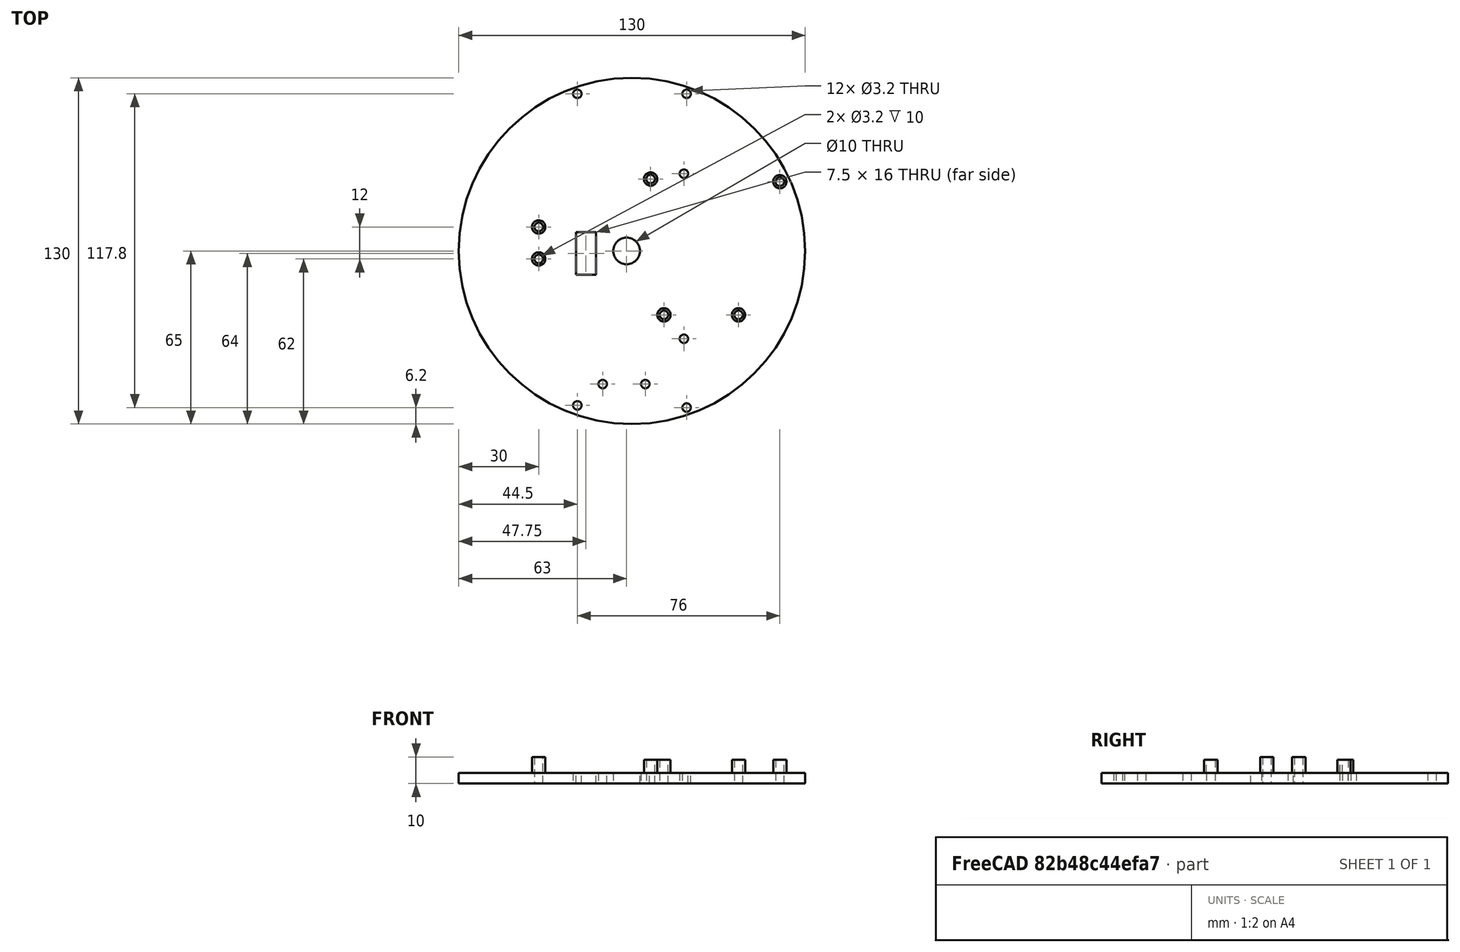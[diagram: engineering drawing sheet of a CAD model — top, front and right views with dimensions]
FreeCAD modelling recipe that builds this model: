
FCSTD DOCUMENT  (FreeCAD 0.21R33668 +26 (Git))
Label: plataformaSuperior
License: All rights reserved
LicenseURL: https://en.wikipedia.org/wiki/All_rights_reserved
objects: Part::Cylinder×26, Part::MultiFuse×10, Part::Cut×6, Part::Box×1, Mesh::Feature×1
note: 43 computed .brp shape members not serialized (recipe doc carries the construction recipe); baked Part::Feature solids carry a one-line shape summary decoded from their .brp

FEATURE [Part::Box] Box027  label="Cubo027"
  AttacherType = Attacher::AttachEngine3D
  Height = 7
  Length = 7.5
  Placement = pos=(-25,-9,46) rot=(0,0,1;0rad)
  Width = 16
FEATURE [Part::Cylinder] Cylinder034  label="Cilindro034"
  Angle = 360
  AttacherType = Attacher::AttachEngine3D
  FirstAngle = 0
  Height = 10
  Placement = pos=(-27,-22,24) rot=(0,0,1;0rad)
  Radius = 1.6
  SecondAngle = 0
FEATURE [Part::Cylinder] Cylinder035  label="Cilindro035"
  Angle = 360
  AttacherType = Attacher::AttachEngine3D
  FirstAngle = 0
  Height = 10
  Placement = pos=(24,11,24) rot=(0,0,1;0rad)
  Radius = 1.6
  SecondAngle = 0
FEATURE [Part::Cylinder] Cylinder036  label="Cilindro036"
  Angle = 360
  AttacherType = Attacher::AttachEngine3D
  FirstAngle = 0
  Height = 10
  Placement = pos=(24,-17,24) rot=(0,0,1;0rad)
  Radius = 1.6
  SecondAngle = 0
FEATURE [Part::Cylinder] Cylinder037  label="Cilindro037"
  Angle = 360
  AttacherType = Attacher::AttachEngine3D
  FirstAngle = 0
  Height = 10
  Placement = pos=(-26,26.5,24) rot=(0,0,1;0rad)
  Radius = 1.6
  SecondAngle = 0
FEATURE [Part::Cylinder] Cylinder038  label="Cilindro038"
  Angle = 360
  AttacherType = Attacher::AttachEngine3D
  FirstAngle = 0
  Height = 6
  Placement = pos=(-27,-22,28) rot=(0,0,1;0rad)
  Radius = 2.5
  SecondAngle = 0
FEATURE [Part::Cylinder] Cylinder039  label="Cilindro039"
  Angle = 360
  AttacherType = Attacher::AttachEngine3D
  FirstAngle = 0
  Height = 6
  Placement = pos=(24,11,28) rot=(0,0,1;0rad)
  Radius = 2.5
  SecondAngle = 0
FEATURE [Part::Cylinder] Cylinder040  label="Cilindro040"
  Angle = 360
  AttacherType = Attacher::AttachEngine3D
  FirstAngle = 0
  Height = 6
  Placement = pos=(24,-17,28) rot=(0,0,1;0rad)
  Radius = 2.5
  SecondAngle = 0
FEATURE [Part::Cylinder] Cylinder041  label="Cilindro041"
  Angle = 360
  AttacherType = Attacher::AttachEngine3D
  FirstAngle = 0
  Height = 6
  Placement = pos=(-26,26.5,28) rot=(0,0,1;0rad)
  Radius = 2.5
  SecondAngle = 0
FEATURE [Part::Cylinder] Cylinder042  label="Cilindro042"
  Angle = 360
  AttacherType = Attacher::AttachEngine3D
  FirstAngle = 0
  Height = 6
  Placement = pos=(35,9,28) rot=(0,0,1;0rad)
  Radius = 2.5
  SecondAngle = 0
FEATURE [Part::Cylinder] Cylinder044  label="Cilindro044"
  Angle = 360
  AttacherType = Attacher::AttachEngine3D
  FirstAngle = 0
  Height = 6
  Placement = pos=(35,-3,28) rot=(0,0,1;0rad)
  Radius = 2.5
  SecondAngle = 0
FEATURE [Part::Cylinder] Cylinder099  label="Cilindro099"
  Angle = 360
  AttacherType = Attacher::AttachEngine3D
  FirstAngle = 0
  Height = 4
  Placement = pos=(-4,0,49) rot=(0,0,1;0rad)
  Radius = 65
  SecondAngle = 0
FEATURE [Part::Cylinder] Cylinder100  label="Cilindro100"
  Angle = 360
  AttacherType = Attacher::AttachEngine3D
  FirstAngle = 0
  Height = 50
  Placement = pos=(16.5,-58.8,-17) rot=(0,0,1;0rad)
  Radius = 1.6
  SecondAngle = 0
FEATURE [Part::Cylinder] Cylinder101  label="Cilindro101"
  Angle = 360
  AttacherType = Attacher::AttachEngine3D
  FirstAngle = 0
  Height = 50
  Placement = pos=(16.5,59,-17) rot=(0,0,1;0rad)
  Radius = 1.6
  SecondAngle = 0
FEATURE [Part::Cylinder] Cylinder102  label="Cilindro102"
  Angle = 360
  AttacherType = Attacher::AttachEngine3D
  FirstAngle = 0
  Height = 50
  Placement = pos=(-24.5,59,-17) rot=(0,0,1;0rad)
  Radius = 1.6
  SecondAngle = 0
FEATURE [Part::Cylinder] Cylinder103  label="Cilindro103"
  Angle = 360
  AttacherType = Attacher::AttachEngine3D
  FirstAngle = 0
  Height = 50
  Placement = pos=(-24.5,-58,-17) rot=(0,0,1;0rad)
  Radius = 1.6
  SecondAngle = 0
FEATURE [Part::Cylinder] Cylinder104  label="Cilindro104"
  Angle = 360
  AttacherType = Attacher::AttachEngine3D
  FirstAngle = 0
  Height = 20
  Placement = pos=(-6,0,43) rot=(0,0,1;0rad)
  Radius = 5
  SecondAngle = 0
FEATURE [Part::Cylinder] Cylinder105  label="Cilindro105"
  Angle = 360
  AttacherType = Attacher::AttachEngine3D
  FirstAngle = 0
  Height = 50
  Placement = pos=(36,-24,43) rot=(0,0,1;0rad)
  Radius = 1.6
  SecondAngle = 0
FEATURE [Part::Cylinder] Cylinder106  label="Cilindro106"
  Angle = 360
  AttacherType = Attacher::AttachEngine3D
  FirstAngle = 0
  Height = 50
  Placement = pos=(8,-24,43) rot=(0,0,1;0rad)
  Radius = 1.6
  SecondAngle = 0
FEATURE [Part::Cylinder] Cylinder107  label="Cilindro107"
  Angle = 360
  AttacherType = Attacher::AttachEngine3D
  FirstAngle = 0
  Height = 50
  Placement = pos=(51.5,26,43) rot=(0,0,1;0rad)
  Radius = 1.6
  SecondAngle = 0
FEATURE [Part::Cylinder] Cylinder108  label="Cilindro108"
  Angle = 360
  AttacherType = Attacher::AttachEngine3D
  FirstAngle = 0
  Height = 50
  Placement = pos=(3,27,43) rot=(0,0,1;0rad)
  Radius = 1.6
  SecondAngle = 0
FEATURE [Part::Cylinder] Cylinder109  label="Cilindro109"
  Angle = 360
  AttacherType = Attacher::AttachEngine3D
  FirstAngle = 0
  Height = 50
  Placement = pos=(15.5,-33,19) rot=(0,0,1;0rad)
  Radius = 1.6
  SecondAngle = 0
FEATURE [Part::Cylinder] Cylinder110  label="Cilindro110"
  Angle = 360
  AttacherType = Attacher::AttachEngine3D
  FirstAngle = 0
  Height = 50
  Placement = pos=(15.5,29,19) rot=(0,0,1;0rad)
  Radius = 1.6
  SecondAngle = 0
FEATURE [Part::Cylinder] Cylinder111  label="Cilindro111"
  Angle = 360
  AttacherType = Attacher::AttachEngine3D
  FirstAngle = 0
  Height = 20
  Placement = pos=(-39,-3,47) rot=(0,0,1;0rad)
  Radius = 1.6
  SecondAngle = 0
FEATURE [Part::Cylinder] Cylinder112  label="Cilindro112"
  Angle = 360
  AttacherType = Attacher::AttachEngine3D
  FirstAngle = 0
  Height = 20
  Placement = pos=(-39,9,47) rot=(0,0,1;0rad)
  Radius = 1.6
  SecondAngle = 0
FEATURE [Part::MultiFuse] Fusion021
  Shapes = -> [Cylinder038,Cylinder039,Cylinder040,Cylinder041]
FEATURE [Part::MultiFuse] Fusion022
  Shapes = -> [Cylinder034,Cylinder035,Cylinder036,Cylinder037]
FEATURE [Part::Cut] Cut014
  Base = -> Fusion021
  Placement = pos=(25,0,24) rot=(0,0,-1;1.5708rad)
  Tool = -> Fusion022
FEATURE [Part::MultiFuse] Fusion028
  Placement = pos=(-74,0,25) rot=(0,0,1;0rad)
  Shapes = -> [Cylinder044,Cylinder042]
FEATURE [Part::MultiFuse] Fusion052  label="taladrosArriba"
  Placement = pos=(0,0,49) rot=(0,0,1;0rad)
  Shapes = -> [Cylinder100,Cylinder101,Cylinder102,Cylinder103]
FEATURE [Part::Cut] Cut015
  Base = -> Cylinder099
  Tool = -> Fusion052
FEATURE [Part::MultiFuse] Fusion053
  Shapes = -> [Cut015,Cut014]
FEATURE [Part::MultiFuse] Fusion054
  Shapes = -> [Cylinder105,Cylinder106,Cylinder107,Cylinder108]
FEATURE [Part::Cut] Cut016
  Base = -> Fusion053
  Tool = -> Fusion054
FEATURE [Part::MultiFuse] Fusion055
  Shapes = -> [Cylinder110,Cylinder109]
FEATURE [Part::Cut] Cut017
  Base = -> Cut016
  Tool = -> Fusion055
FEATURE [Part::MultiFuse] Fusion056
  Shapes = -> [Box027,Cylinder104,Cylinder111,Cylinder112]
FEATURE [Part::MultiFuse] Fusion057
  Shapes = -> [Cut017,Fusion028]
FEATURE [Part::Cut] Cut018  label="plataformaS"
  Base = -> Fusion057
  Tool = -> Fusion056
FEATURE [Part::Cylinder] Cylinder  label="Cilindro"
  Angle = 360
  AttacherType = Attacher::AttachEngine3D
  FirstAngle = 0
  Height = 10
  Placement = pos=(-15,-50,45) rot=(0,0,1;0rad)
  Radius = 1.6
  SecondAngle = 0
FEATURE [Part::Cylinder] Cylinder113  label="Cilindro113"
  Angle = 360
  AttacherType = Attacher::AttachEngine3D
  FirstAngle = 0
  Height = 10
  Placement = pos=(1,-50,45) rot=(0,0,1;0rad)
  Radius = 1.6
  SecondAngle = 0
FEATURE [Part::MultiFuse] Fusion
  Shapes = -> [Cylinder113,Cylinder]
FEATURE [Part::Cut] Cut  label="plataformaSuperior"
  Base = -> Cut018
  Tool = -> Fusion
FEATURE [Mesh::Feature] Mesh  label="plataformaSuperior (Meshed)"
